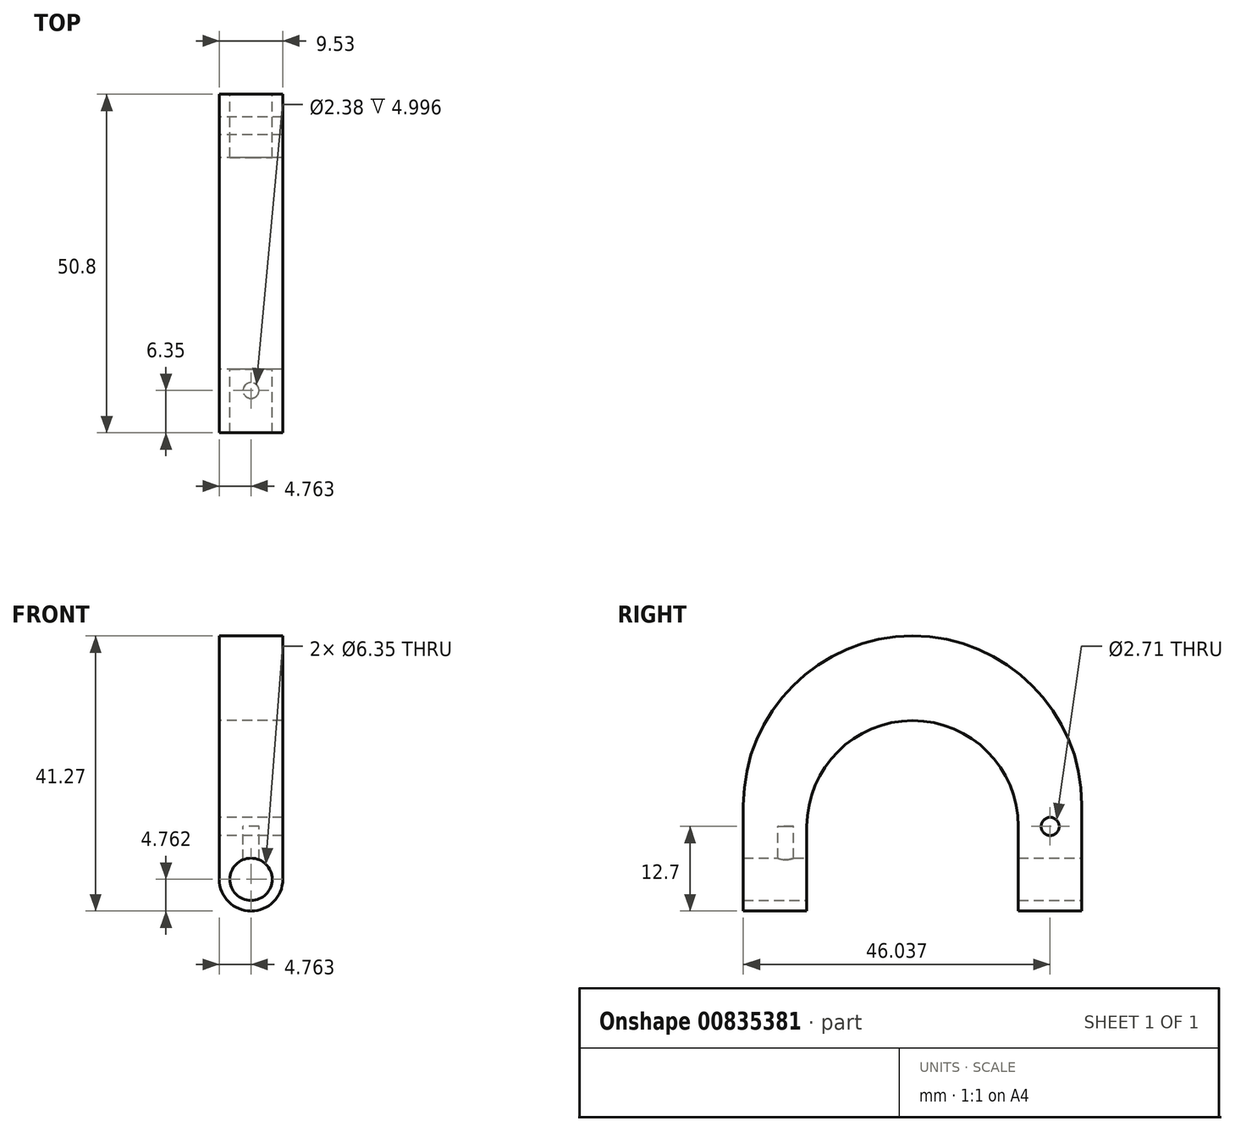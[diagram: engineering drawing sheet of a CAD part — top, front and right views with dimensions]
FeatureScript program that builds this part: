
annotation { "Feature Type Name" : "Feature", "Feature Type Description" : "" }
export const myFeature = defineFeature(function(context is Context, id is Id, definition is map)
    precondition{}
    {
        {
            var Q0;
            Q0=qCreatedBy(makeId("Right.planeOp"),FACE);
            var sketch = newSketch(context, id + "F0", { "sketchPlane" : qUnion([Q0])});
            skLineSegment(sketch, "E0", {"start": v(-15.88, 0) * mm, "end": v(-15.88, -12.7) * mm});
            skLineSegment(sketch, "E1", {"start": v(-15.88, -12.7) * mm, "end": v(-25.4, -12.7) * mm});
            skLineSegment(sketch, "E2", {"start": v(-25.4, -12.7) * mm, "end": v(-25.4, 0) * mm});
            skLineSegment(sketch, "E3", {"start": v(15.88, 0) * mm, "end": v(15.88, -12.7) * mm});
            skLineSegment(sketch, "E4", {"start": v(15.88, -12.7) * mm, "end": v(25.4, -12.7) * mm});
            skLineSegment(sketch, "E5", {"start": v(25.4, -12.7) * mm, "end": v(25.4, 0) * mm});
            skLineSegment(sketch, "E6", {"start": v(-25.4, 0) * mm, "end": v(-25.4, 3.18) * mm});
            skLineSegment(sketch, "E7", {"start": v(0, 28.58) * mm, "end": v(0, 28.58) * mm});
            skLineSegment(sketch, "E8", {"start": v(25.4, 3.18) * mm, "end": v(25.4, 0) * mm});
            skLineSegment(sketch, "E9", {"start": v(15.88, 0) * mm, "end": v(15.88, 0) * mm});
            skLineSegment(sketch, "E10", {"start": v(0, 15.88) * mm, "end": v(0, 15.88) * mm});
            skLineSegment(sketch, "E11", {"start": v(-15.88, 0) * mm, "end": v(-15.88, 0) * mm});
            skLineSegment(sketch, "E12", {"start": v(0, 0) * mm, "end": v(0, 15.88) * mm});
            skPoint(sketch, "E13.visualSharp", {"position": v(15.88, 15.88) * mm});
            skArc(sketch, "E13.filletArc", {"start": v(15.88, 0) * mm, "mid": v(11.23, 11.23) * mm, "end": v(0, 15.88) * mm});
            skPoint(sketch, "E14.visualSharp", {"position": v(-15.88, 15.88) * mm});
            skArc(sketch, "E14.filletArc", {"start": v(0, 15.88) * mm, "mid": v(-11.23, 11.23) * mm, "end": v(-15.88, 0) * mm});
            skPoint(sketch, "E15.visualSharp", {"position": v(25.4, 28.58) * mm});
            skArc(sketch, "E15.filletArc", {"start": v(25.4, 3.18) * mm, "mid": v(17.96, 21.14) * mm, "end": v(0, 28.58) * mm});
            skPoint(sketch, "E16.visualSharp", {"position": v(-25.4, 28.58) * mm});
            skArc(sketch, "E16.filletArc", {"start": v(0, 28.58) * mm, "mid": v(-17.96, 21.14) * mm, "end": v(-25.4, 3.18) * mm});
            skCircle(sketch, "E17", {"center": v(20.64, 0) * mm, "radius": 1.35 * mm});
            skPoint(sketch, "E18", {"position": v(20.64, -12.7) * mm});
            skSolve(sketch);
        }
        {
            var Q0;
            Q0=makeQuery(id+"F0.imprint","IMPRINT",FACE,{"disambiguationData":[TD([[makeQuery(id+"F0.imprint","IMPRINT",EDGE,{"derivedFrom":sQuery(id+"F0.wireOp",EDGE,"yir4HEj7-XJFo-UCWM-mcmq-spvEDfUMwMPs")}),1.0]])]});
            var Q1;
            {var subQ3=sQuery(id+"F0.wireOp",EDGE,"E2");Q1=makeQuery(id+"F0.imprint","IMPRINT",FACE,{"disambiguationData":[TD([[makeQuery(id+"F0.imprint","IMPRINT",EDGE,{"derivedFrom":subQ3}),-1.0]])]});}
            var Q2;
            {var subQ5=sQuery(id+"F0.wireOp",EDGE,"E0");Q2=makeQuery(id+"F0.imprint","IMPRINT",FACE,{"disambiguationData":[TD([[makeQuery(id+"F0.imprint","IMPRINT",EDGE,{"derivedFrom":subQ5}),-1.0]])]});}
            var Q3;
            {var subQ3=sQuery(id+"F0.wireOp",EDGE,"E5");Q3=makeQuery(id+"F0.imprint","IMPRINT",FACE,{"disambiguationData":[TD([[makeQuery(id+"F0.imprint","IMPRINT",EDGE,{"derivedFrom":subQ3}),1.0]])]});}
            extrude(context, id + "F1", {"entities" : qUnion([Q0, Q1, Q2, Q3]), "depth" : 9.52 * mm, "offsetDistance" : 25.4 * mm});
        }
        {
            var Q0;
            Q0=makeQuery(id+"F1.opExtrude","SWEPT_FACE",FACE,{"disambiguationData":[OSD([sQuery(id+"F0.wireOp",EDGE,"E5")])]});
            var sketch = newSketch(context, id + "F2", { "sketchPlane" : qUnion([Q0])});
            skCircle(sketch, "E19", {"center": v(-4.76, -7.94) * mm, "radius": 3.18 * mm});
            skArc(sketch, "E20", {"start": v(-9.53, -7.94) * mm, "mid": v(-4.76, -12.7) * mm, "end": v(0, -7.94) * mm});
            skLineSegment(sketch, "E21", {"start": v(-9.53, -7.94) * mm, "end": v(-9.53, -12.7) * mm});
            skLineSegment(sketch, "E22", {"start": v(0, -7.94) * mm, "end": v(0, -12.7) * mm});
            skLineSegment(sketch, "E23", {"start": v(-9.53, -12.7) * mm, "end": v(0, -12.7) * mm, "construction": true});
            skLineSegment(sketch, "E24", {"start": v(0, -12.7) * mm, "end": v(-9.53, -12.7) * mm, "construction": true});
            skSolve(sketch);
        }
        {
            var Q0;
            Q0=makeQuery(id+"F2.imprint","IMPRINT",FACE,{"disambiguationData":[TD([[makeQuery(id+"F2.imprint","IMPRINT",EDGE,{"derivedFrom":sQuery(id+"F2.wireOp",EDGE,"E19")}),1.0]])]});
            var Q1;
            {var subQ0=sQuery(id+"F2.wireOp",EDGE,"E21");Q1=makeQuery(id+"F2.imprint","IMPRINT",FACE,{"disambiguationData":[TD([[makeQuery(id+"F2.imprint","IMPRINT",EDGE,{"derivedFrom":subQ0}),-1.0]])]});}
            var Q2;
            {var subQ0=sQuery(id+"F2.wireOp",EDGE,"E22");Q2=makeQuery(id+"F2.imprint","IMPRINT",FACE,{"disambiguationData":[TD([[makeQuery(id+"F2.imprint","IMPRINT",EDGE,{"derivedFrom":subQ0}),1.0]])]});}
            extrude(context, id + "F3", {"entities" : qUnion([Q0, Q1, Q2]), "operationType" : NewBodyOperationType.REMOVE, "oppositeDirection" : true, "depth" : 50.8 * mm, "offsetDistance" : 25.4 * mm});
        }
        {
            var Q0;
            Q0=qCreatedBy(makeId("Top.planeOp"),FACE);
            var sketch = newSketch(context, id + "F4", { "sketchPlane" : qUnion([Q0])});
            skLineSegment(sketch, "E25", {"start": v(0, -22.23) * mm, "end": v(9.53, -22.23) * mm, "construction": true});
            skLineSegment(sketch, "E26", {"start": v(0, -15.88) * mm, "end": v(9.53, -15.88) * mm, "construction": true});
            skLineSegment(sketch, "E27", {"start": v(0, -15.88) * mm, "end": v(9.52, -22.23) * mm, "construction": true});
            skLineSegment(sketch, "E28", {"start": v(0, -22.23) * mm, "end": v(9.53, -15.88) * mm, "construction": true});
            skCircle(sketch, "E29", {"center": v(4.76, -19.05) * mm, "radius": 1.2 * mm});
            skSolve(sketch);
        }
        {
            var Q0;
            Q0 = qSketchRegion(id + "F4", true);
            extrude(context, id + "F5", {"entities" : qUnion([Q0]), "operationType" : NewBodyOperationType.REMOVE, "oppositeDirection" : true, "depth" : 6.35 * mm, "offsetDistance" : 25.4 * mm});
        }
    });
